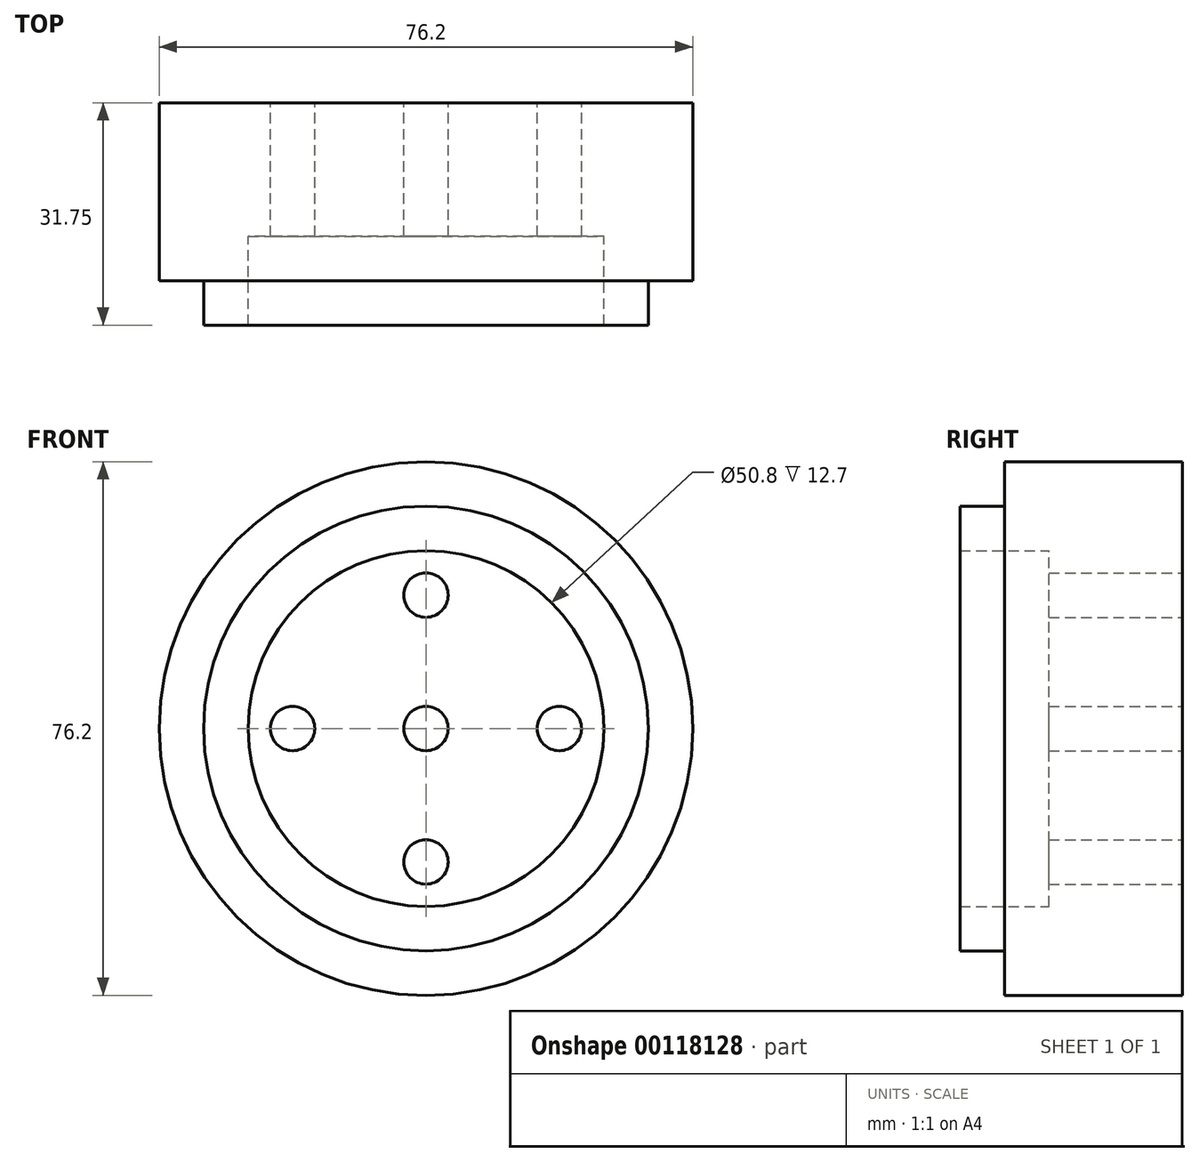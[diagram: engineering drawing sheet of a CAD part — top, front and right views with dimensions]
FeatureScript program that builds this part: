
annotation { "Feature Type Name" : "Feature", "Feature Type Description" : "" }
export const myFeature = defineFeature(function(context is Context, id is Id, definition is map)
    precondition{}
    {
        {
            var Q0;
            Q0=qCreatedBy(makeId("Front.planeOp"),FACE);
            var sketch = newSketch(context, id + "F0", { "sketchPlane" : qUnion([Q0])});
            skCircle(sketch, "E0", {"center": v(0, 0) * mm, "radius": 38.1 * mm});
            skCircle(sketch, "E1", {"center": v(0, 0) * mm, "radius": 31.75 * mm});
            skCircle(sketch, "E2", {"center": v(0, 0) * mm, "radius": 25.4 * mm});
            skCircle(sketch, "E3", {"center": v(0, 0) * mm, "radius": 19.05 * mm, "construction": true});
            skCircle(sketch, "E4", {"center": v(0, 19.05) * mm, "radius": 3.18 * mm});
            skCircle(sketch, "E5.1.0", {"center": v(-19.05, 0) * mm, "radius": 3.18 * mm});
            skCircle(sketch, "E5.2.0", {"center": v(0, -19.05) * mm, "radius": 3.18 * mm});
            skCircle(sketch, "E5.3.0", {"center": v(19.05, 0) * mm, "radius": 3.18 * mm});
            skCircle(sketch, "E6", {"center": v(0, 0) * mm, "radius": 3.18 * mm});
            skSolve(sketch);
        }
        {
            var Q0;
            Q0=makeQuery(id+"F0.imprint","IMPRINT",FACE,{"disambiguationData":[TD([[makeQuery(id+"F0.imprint","IMPRINT",EDGE,{"derivedFrom":sQuery(id+"F0.wireOp",EDGE,"E0")}),1.0]])]});
            extrude(context, id + "F1", {"entities" : qUnion([Q0]), "depth" : 25.4 * mm});
        }
        {
            var Q0;
            Q0=makeQuery(id+"F0.imprint","IMPRINT",FACE,{"disambiguationData":[TD([[makeQuery(id+"F0.imprint","IMPRINT",EDGE,{"derivedFrom":sQuery(id+"F0.wireOp",EDGE,"E1")}),1.0]])]});
            extrude(context, id + "F2", {"entities" : qUnion([Q0]), "operationType" : NewBodyOperationType.ADD, "depth" : 31.75 * mm});
        }
        {
            var Q0;
            Q0=makeQuery(id+"F0.imprint","IMPRINT",FACE,{"disambiguationData":[TD([[makeQuery(id+"F0.imprint","IMPRINT",EDGE,{"derivedFrom":sQuery(id+"F0.wireOp",EDGE,"E2")}),1.0]])]});
            extrude(context, id + "F3", {"entities" : qUnion([Q0]), "operationType" : NewBodyOperationType.ADD, "depth" : 19.05 * mm});
        }
    });
